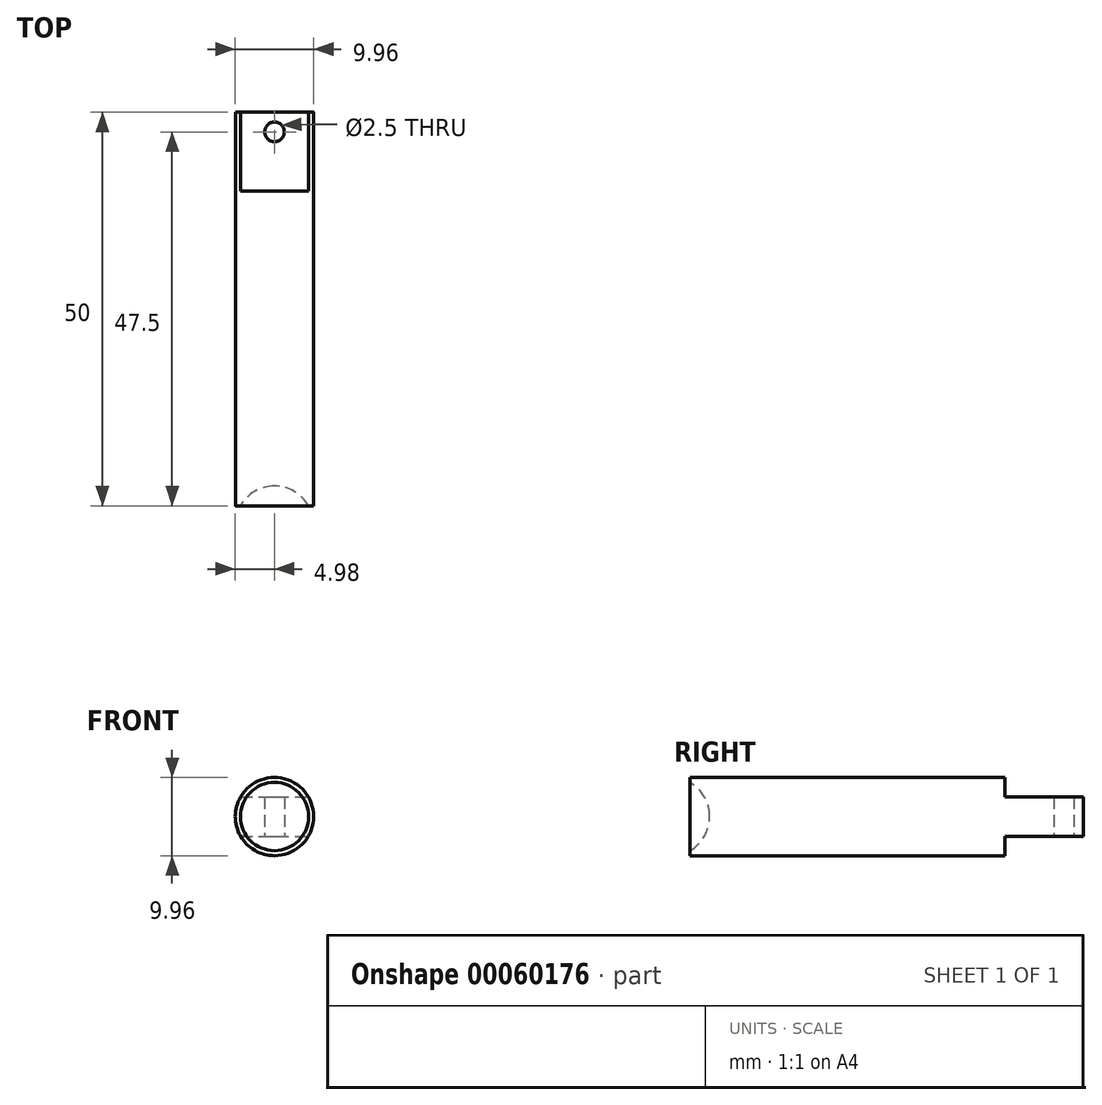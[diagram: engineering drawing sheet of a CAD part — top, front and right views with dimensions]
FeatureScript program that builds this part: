
annotation { "Feature Type Name" : "Feature", "Feature Type Description" : "" }
export const myFeature = defineFeature(function(context is Context, id is Id, definition is map)
    precondition{}
    {
        {
            var Q0;
            Q0=qCreatedBy(makeId("Front.planeOp"),FACE);
            var sketch = newSketch(context, id + "F0", { "sketchPlane" : qUnion([Q0])});
            skCircle(sketch, "E0", {"center": v(0, 0) * mm, "radius": 4.98 * mm});
            skSolve(sketch);
        }
        {
            var Q0;
            Q0=qSketchRegion(id+"F0",true);
            extrude(context, id + "F1", {"entities" : qUnion([Q0]), "depth" : 50 * mm});
        }
        {
            var Q0;
            Q0=qCreatedBy(makeId("Right.planeOp"),FACE);
            var sketch = newSketch(context, id + "F2", { "sketchPlane" : qUnion([Q0])});
            skArc(sketch, "E1", {"start": v(-47.5, 0) * mm, "mid": v(-48.17, 2.5) * mm, "end": v(-50, 4.33) * mm});
            skLineSegment(sketch, "E2", {"start": v(-50, 4.33) * mm, "end": v(-52.5, 0) * mm});
            skLineSegment(sketch, "E3", {"start": v(-52.5, 0) * mm, "end": v(-47.5, 0) * mm});
            skPoint(sketch, "E4.orphan", {"position": v(-50, -4.33) * mm});
            skSolve(sketch);
        }
        {
            var Q0;
            Q0=qSketchRegion(id+"F2",true);
            var Q1;
            Q1=sQuery(id+"F2.wireOp",EDGE,"E3");
            revolve(context, id + "F3", {"operationType" : NewBodyOperationType.REMOVE, "entities" : qUnion([Q0]), "axis" : qUnion([Q1]), "revolveType" : RevolveType.FULL, "oppositeDirection" : true});
        }
        {
            var Q0;
            Q0=qCreatedBy(makeId("Right.planeOp"),FACE);
            var sketch = newSketch(context, id + "F4", { "sketchPlane" : qUnion([Q0])});
            skLineSegment(sketch, "E5.bottom", {"start": v(-10, 33.44) * mm, "end": v(26.94, 33.44) * mm});
            skLineSegment(sketch, "E5.top", {"start": v(-10, 2.5) * mm, "end": v(26.94, 2.5) * mm});
            skLineSegment(sketch, "E5.left", {"start": v(-10, 33.44) * mm, "end": v(-10, 2.5) * mm});
            skLineSegment(sketch, "E5.right", {"start": v(26.94, 33.44) * mm, "end": v(26.94, 2.5) * mm});
            skLineSegment(sketch, "E6.bottom", {"start": v(-10, -2.5) * mm, "end": v(26.96, -2.5) * mm});
            skLineSegment(sketch, "E6.top", {"start": v(-10, -54.36) * mm, "end": v(26.96, -54.36) * mm});
            skLineSegment(sketch, "E6.left", {"start": v(-10, -2.5) * mm, "end": v(-10, -54.36) * mm});
            skLineSegment(sketch, "E6.right", {"start": v(26.96, -2.5) * mm, "end": v(26.96, -54.36) * mm});
            skSolve(sketch);
        }
        {
            var Q0;
            Q0=qSketchRegion(id+"F4",true);
            extrude(context, id + "F5", {"entities" : qUnion([Q0]), "operationType" : NewBodyOperationType.REMOVE, "endBound" : BoundingType.THROUGH_ALL, "oppositeDirection" : true, "depth" : 25 * mm, "hasSecondDirection" : true, "secondDirectionBound" : BoundingType.THROUGH_ALL, "secondDirectionOppositeDirection" : false, "secondDirectionDepth" : 25 * mm});
        }
        {
            var Q0;
            Q0=makeQuery(id+"F5.boolean.opBoolean","COPY",FACE,{"derivedFrom":makeQuery(id+"F5.opExtrude","SWEPT_FACE",FACE,{"disambiguationData":[OSD([sQuery(id+"F4.wireOp",EDGE,"E6.bottom")])]})});
            var sketch = newSketch(context, id + "F6", { "sketchPlane" : qUnion([Q0])});
            skCircle(sketch, "E7", {"center": v(0, 2.5) * mm, "radius": 1.25 * mm});
            skSolve(sketch);
        }
        {
            var Q0;
            Q0=qSketchRegion(id+"F6",true);
            extrude(context, id + "F7", {"entities" : qUnion([Q0]), "operationType" : NewBodyOperationType.REMOVE, "oppositeDirection" : true, "depth" : 25 * mm});
        }
    });
